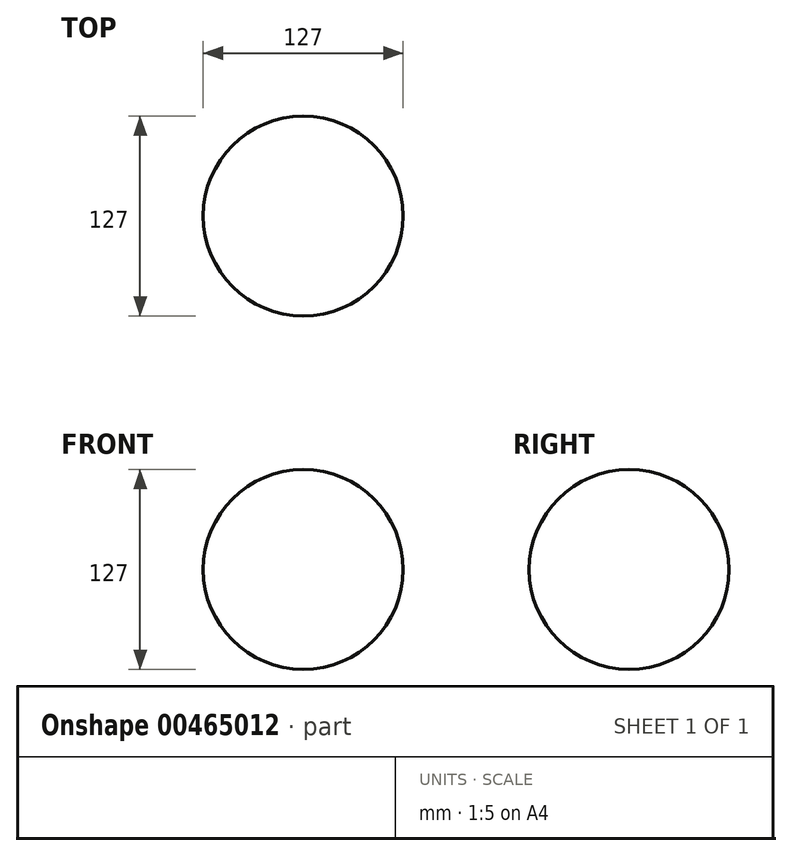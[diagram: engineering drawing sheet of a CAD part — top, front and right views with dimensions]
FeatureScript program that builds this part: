
annotation { "Feature Type Name" : "Feature", "Feature Type Description" : "" }
export const myFeature = defineFeature(function(context is Context, id is Id, definition is map)
    precondition{}
    {
        {
            var Q0;
            Q0=qCreatedBy(makeId("Right.planeOp"),FACE);
            var sketch = newSketch(context, id + "F0", { "sketchPlane" : qUnion([Q0])});
            skCircle(sketch, "E0", {"center": v(0, 0) * mm, "radius": 63.5 * mm});
            skLineSegment(sketch, "E1.bottom", {"start": v(-25.4, -93.12) * mm, "end": v(-38.1, -93.12) * mm});
            skLineSegment(sketch, "E1.top", {"start": v(-25.4, -58.2) * mm, "end": v(-38.1, -58.2) * mm});
            skLineSegment(sketch, "E1.left", {"start": v(-25.4, -93.12) * mm, "end": v(-25.4, -58.2) * mm});
            skLineSegment(sketch, "E1.right", {"start": v(-38.1, -93.12) * mm, "end": v(-38.1, -58.2) * mm});
            skLineSegment(sketch, "E2.MirrorCS", {"start": v(38.1, -93.12) * mm, "end": v(38.1, -58.2) * mm});
            skLineSegment(sketch, "E3.MirrorCS", {"start": v(25.4, -93.12) * mm, "end": v(25.4, -58.2) * mm});
            skLineSegment(sketch, "E4.MirrorCS", {"start": v(25.4, -93.12) * mm, "end": v(38.1, -93.12) * mm});
            skLineSegment(sketch, "E5.MirrorCS", {"start": v(25.4, -58.2) * mm, "end": v(38.1, -58.2) * mm});
            skLineSegment(sketch, "E6.bottom", {"start": v(-38.1, -93.12) * mm, "end": v(-50.8, -93.12) * mm});
            skLineSegment(sketch, "E6.top", {"start": v(-38.1, -50.8) * mm, "end": v(-50.8, -50.8) * mm});
            skLineSegment(sketch, "E6.left", {"start": v(-38.1, -93.12) * mm, "end": v(-38.1, -50.8) * mm});
            skLineSegment(sketch, "E6.right", {"start": v(-50.8, -93.12) * mm, "end": v(-50.8, -50.8) * mm});
            skLineSegment(sketch, "E7.MirrorCS", {"start": v(38.1, -93.12) * mm, "end": v(50.8, -93.12) * mm});
            skLineSegment(sketch, "E8.MirrorCS", {"start": v(50.8, -93.12) * mm, "end": v(50.8, -50.8) * mm});
            skLineSegment(sketch, "E9.MirrorCS", {"start": v(38.1, -93.12) * mm, "end": v(38.1, -50.8) * mm});
            skLineSegment(sketch, "E10.MirrorCS", {"start": v(38.1, -50.8) * mm, "end": v(50.8, -50.8) * mm});
            skLineSegment(sketch, "E11", {"start": v(0, 63.5) * mm, "end": v(0, -63.5) * mm});
            skPoint(sketch, "E12", {"position": v(0, 63.5) * mm});
            skLineSegment(sketch, "E13.bottom", {"start": v(-24.83, 165.1) * mm, "end": v(25.97, 165.1) * mm});
            skLineSegment(sketch, "E13.top", {"start": v(-24.83, 63.5) * mm, "end": v(25.97, 63.5) * mm});
            skLineSegment(sketch, "E13.left", {"start": v(-24.83, 165.1) * mm, "end": v(-24.83, 63.5) * mm});
            skLineSegment(sketch, "E13.right", {"start": v(25.97, 165.1) * mm, "end": v(25.97, 63.5) * mm});
            skPoint(sketch, "E14", {"position": v(25.97, 114.3) * mm});
            skSolve(sketch);
        }
        {
            var Q0;
            {var subQ4=sQuery(id+"F0.wireOp",EDGE,"E11");Q0=makeQuery(id+"F0.imprint","IMPRINT",FACE,{"disambiguationData":[TD([[makeQuery(id+"F0.imprint","IMPRINT",EDGE,{"derivedFrom":subQ4}),1.0]])]});}
            var Q1;
            Q1=sQuery(id+"F0.wireOp",EDGE,"E11");
            revolve(context, id + "F1", {"entities" : qUnion([Q0]), "axis" : qUnion([Q1]), "revolveType" : RevolveType.ONE_DIRECTION, "angle" : 360 * degree});
        }
    });
